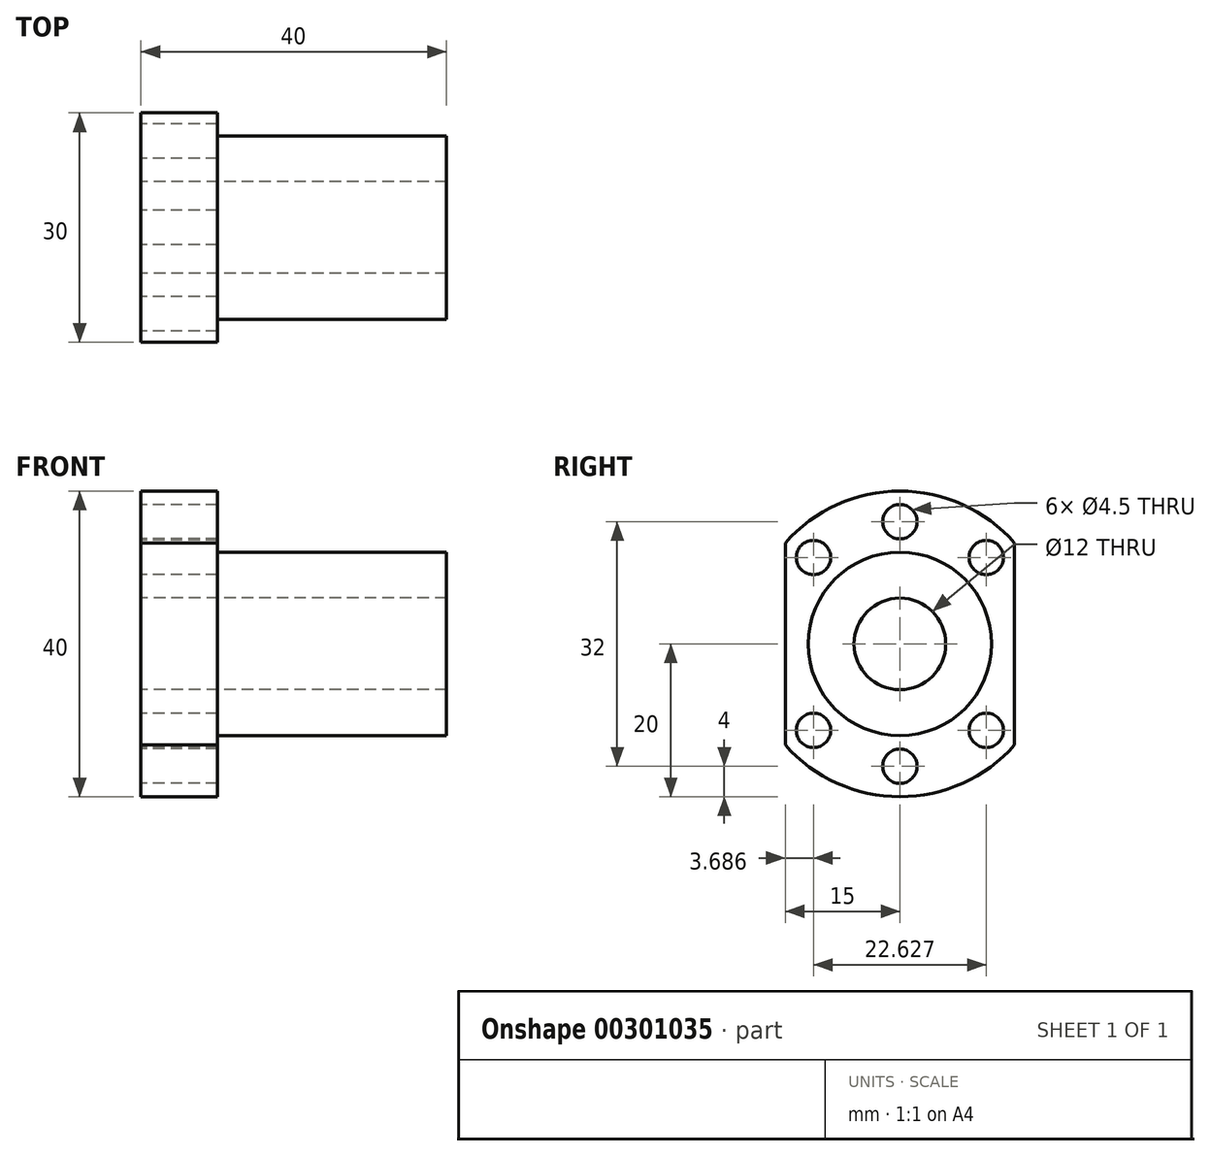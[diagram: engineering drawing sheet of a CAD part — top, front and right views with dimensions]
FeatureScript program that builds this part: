
annotation { "Feature Type Name" : "Feature", "Feature Type Description" : "" }
export const myFeature = defineFeature(function(context is Context, id is Id, definition is map)
    precondition{}
    {
        {
            var Q0;
            Q0=qCreatedBy(makeId("Front.planeOp"),FACE);
            var sketch = newSketch(context, id + "F0", { "sketchPlane" : qUnion([Q0])});
            skLineSegment(sketch, "E0", {"start": v(0, 0) * mm, "end": v(48.43, 0) * mm, "construction": true});
            skLineSegment(sketch, "E1", {"start": v(0, 6) * mm, "end": v(0, 20) * mm});
            skLineSegment(sketch, "E2", {"start": v(0, 20) * mm, "end": v(10, 20) * mm});
            skLineSegment(sketch, "E3", {"start": v(10, 20) * mm, "end": v(10, 12) * mm});
            skLineSegment(sketch, "E4", {"start": v(10, 12) * mm, "end": v(40, 12) * mm});
            skLineSegment(sketch, "E5", {"start": v(40, 12) * mm, "end": v(40, 6) * mm});
            skLineSegment(sketch, "E6", {"start": v(40, 6) * mm, "end": v(0, 6) * mm});
            skSolve(sketch);
        }
        {
            var Q0;
            Q0 = qSketchRegion(id + "F0", true);
            var Q1;
            Q1=sQuery(id+"F0.wireOp",EDGE,"E0");
            revolve(context, id + "F1", {"entities" : qUnion([Q0]), "axis" : qUnion([Q1]), "revolveType" : RevolveType.FULL});
        }
        {
            var Q0;
            Q0=makeQuery(id+"F1.opRevolve","SWEPT_FACE",FACE,{"disambiguationData":[OSD([sQuery(id+"F0.wireOp",EDGE,"E1")])]});
            var sketch = newSketch(context, id + "F2", { "sketchPlane" : qUnion([Q0])});
            skLineSegment(sketch, "E7", {"start": v(0, 0) * mm, "end": v(0, 27.72) * mm, "construction": true});
            skLineSegment(sketch, "E8", {"start": v(-15, 20) * mm, "end": v(-15, -20) * mm});
            skLineSegment(sketch, "E9", {"start": v(-15, -20) * mm, "end": v(-25, -20) * mm});
            skLineSegment(sketch, "E10", {"start": v(-25, -20) * mm, "end": v(-25, 20) * mm});
            skLineSegment(sketch, "E11", {"start": v(-25, 20) * mm, "end": v(-15, 20) * mm});
            skLineSegment(sketch, "E12", {"start": v(15, 20) * mm, "end": v(15, -20) * mm});
            skLineSegment(sketch, "E13", {"start": v(15, -20) * mm, "end": v(25, -20) * mm});
            skLineSegment(sketch, "E14", {"start": v(25, -20) * mm, "end": v(25, 20) * mm});
            skLineSegment(sketch, "E15", {"start": v(25, 20) * mm, "end": v(15, 20) * mm});
            skCircle(sketch, "E16", {"center": v(0, 0) * mm, "radius": 16 * mm, "construction": true});
            skLineSegment(sketch, "E17", {"start": v(-11.31, 11.31) * mm, "end": v(11.31, -11.31) * mm, "construction": true});
            skLineSegment(sketch, "E18", {"start": v(11.31, 11.31) * mm, "end": v(-11.31, -11.31) * mm, "construction": true});
            skLineSegment(sketch, "E19", {"start": v(0, 0) * mm, "end": v(0, -16) * mm, "construction": true});
            skLineSegment(sketch, "E20", {"start": v(0, 0) * mm, "end": v(-27.35, 0) * mm, "construction": true});
            skPoint(sketch, "E21", {"position": v(-11.31, 11.31) * mm});
            skPoint(sketch, "E22", {"position": v(11.31, 11.31) * mm});
            skPoint(sketch, "E23", {"position": v(-11.31, -11.31) * mm});
            skPoint(sketch, "E24", {"position": v(11.31, -11.31) * mm});
            skPoint(sketch, "E25", {"position": v(0, 16) * mm});
            skPoint(sketch, "E26", {"position": v(0, -16) * mm});
            skSolve(sketch);
        }
        {
            var Q0;
            Q0 = qSketchRegion(id + "F2", true);
            extrude(context, id + "F3", {"entities" : qUnion([Q0]), "operationType" : NewBodyOperationType.REMOVE, "endBound" : BoundingType.THROUGH_ALL, "oppositeDirection" : true, "depth" : 25 * mm});
        }
        {
            var Q0;
            Q0=sQuery(id+"F2.wireOp",VERTEX,"E21");
            var Q1;
            Q1=sQuery(id+"F2.wireOp",VERTEX,"E22");
            var Q2;
            Q2=sQuery(id+"F2.wireOp",VERTEX,"E24");
            var Q3;
            Q3=sQuery(id+"F2.wireOp",VERTEX,"E23");
            var Q4;
            Q4=sQuery(id+"F2.wireOp",VERTEX,"E25");
            var Q5;
            Q5=sQuery(id+"F2.wireOp",VERTEX,"E26");
            var Q6;
            Q6=makeQuery(id+"F1.opRevolve","SWEPT_BODY",BODY,{"disambiguationData":[OSD([sQuery(id+"F0.wireOp",EDGE,"E1"),sQuery(id+"F0.wireOp",EDGE,"E2"),sQuery(id+"F0.wireOp",EDGE,"E3"),sQuery(id+"F0.wireOp",EDGE,"E4"),sQuery(id+"F0.wireOp",EDGE,"E5"),sQuery(id+"F0.wireOp",EDGE,"E6")])]});
            hole(context, id + "F4", {"style" : HoleStyle.SIMPLE, "endStyle" : HoleEndStyle.THROUGH, "standardTappedOrClearance" : lookupTablePath({ "standard" : "ISO", "size" : "4.5", "type" : "Drilled" }), "standardBlindInLast" : lookupTablePath({ "standard" : "ISO", "size" : "4.5", "type" : "Drilled" }), "holeDiameter" : 4.5 * mm, "tappedDepth" : 8 * mm, "tapClearance" : 3, "locations" : qUnion([Q0, Q1, Q2, Q3, Q4, Q5]), "scope" : qUnion([Q6])});
        }
    });
